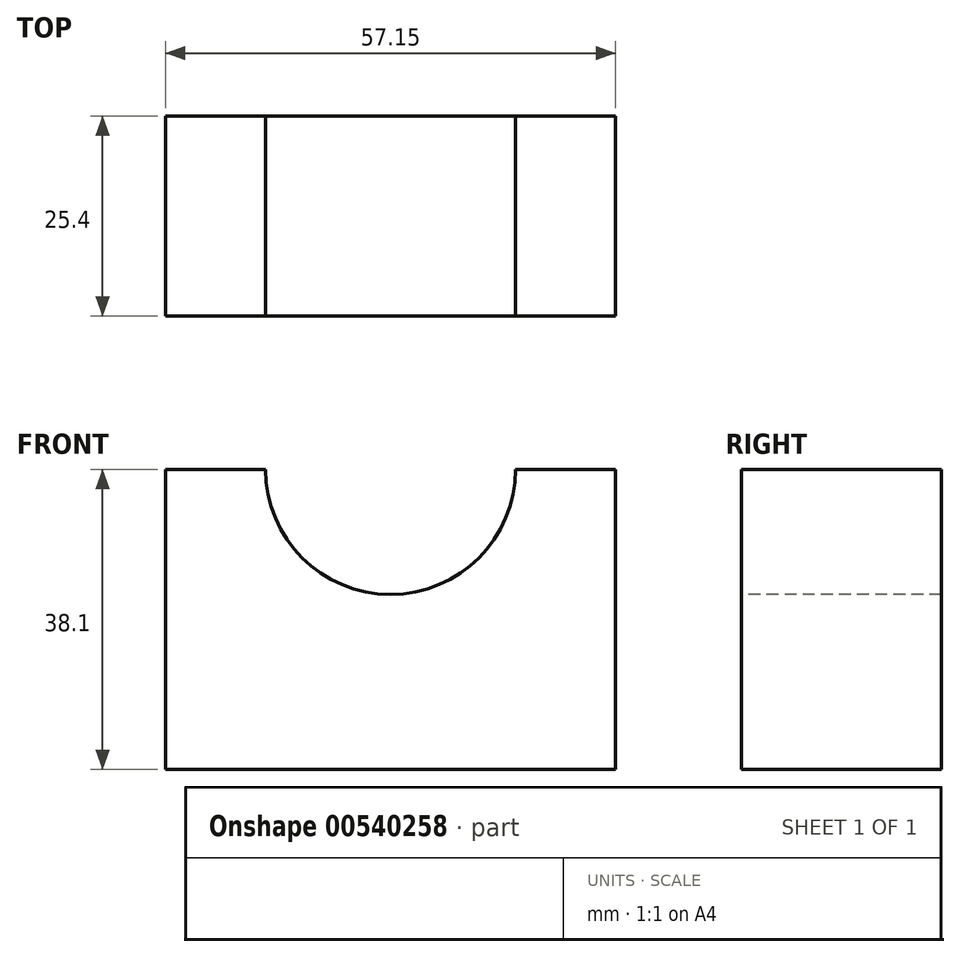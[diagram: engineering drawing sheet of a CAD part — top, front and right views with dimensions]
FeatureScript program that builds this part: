
annotation { "Feature Type Name" : "Feature", "Feature Type Description" : "" }
export const myFeature = defineFeature(function(context is Context, id is Id, definition is map)
    precondition{}
    {
        {
            var Q0;
            Q0=qCreatedBy(makeId("Front.planeOp"),FACE);
            var sketch = newSketch(context, id + "F0", { "sketchPlane" : qUnion([Q0])});
            skLineSegment(sketch, "E0", {"start": v(0, 0) * mm, "end": v(-57.15, 0) * mm});
            skLineSegment(sketch, "E1", {"start": v(-57.15, 0) * mm, "end": v(-57.15, 38.1) * mm});
            skLineSegment(sketch, "E2", {"start": v(-57.15, 38.1) * mm, "end": v(0, 38.1) * mm});
            skLineSegment(sketch, "E3", {"start": v(0, 38.1) * mm, "end": v(0, 0) * mm});
            skArc(sketch, "E4", {"start": v(-44.45, 38.1) * mm, "mid": v(-28.57, 22.22) * mm, "end": v(-12.7, 38.1) * mm});
            skSolve(sketch);
        }
        {
            var Q0;
            {var subQ0=sQuery(id+"F0.wireOp",EDGE,"E4");Q0=makeQuery(id+"F0.imprint","IMPRINT",FACE,{"disambiguationData":[TD([[makeQuery(id+"F0.imprint","IMPRINT",EDGE,{"derivedFrom":subQ0}),1.0]])]});}
            var Q1;
            Q1=makeQuery(id+"F0.imprint","IMPRINT",FACE,{"disambiguationData":[TD([[makeQuery(id+"F0.imprint","IMPRINT",EDGE,{"derivedFrom":sQuery(id+"F0.wireOp",EDGE,"E0")}),-1.0]])]});
            extrude(context, id + "F1", {"entities" : qUnion([Q0, Q1]), "depth" : 25.4 * mm, "offsetDistance" : 25.4 * mm});
        }
        {
            var Q0;
            Q0=makeQuery(id+"F1.opExtrude","CAP_FACE",FACE,{"disambiguationData":[OSD([sQuery(id+"F0.wireOp",EDGE,"E0"),sQuery(id+"F0.wireOp",EDGE,"E1"),sQuery(id+"F0.wireOp",EDGE,"E2"),sQuery(id+"F0.wireOp",EDGE,"E3")])],"isStart":false});
            var sketch = newSketch(context, id + "F2", { "sketchPlane" : qUnion([Q0])});
            skArc(sketch, "E5", {"start": v(-44.45, 38.1) * mm, "mid": v(-28.57, 22.22) * mm, "end": v(-12.7, 38.1) * mm});
            skSolve(sketch);
        }
        {
            var Q0;
            {var subQ0=sQuery(id+"F2.wireOp",EDGE,"E5");Q0=makeQuery(id+"F2.imprint","IMPRINT",FACE,{"disambiguationData":[TD([[makeQuery(id+"F2.imprint","IMPRINT",EDGE,{"derivedFrom":subQ0}),1.0]])]});}
            extrude(context, id + "F3", {"entities" : qUnion([Q0]), "operationType" : NewBodyOperationType.REMOVE, "endBound" : BoundingType.THROUGH_ALL, "oppositeDirection" : true, "depth" : 25.4 * mm, "offsetDistance" : 25.4 * mm});
        }
    });
